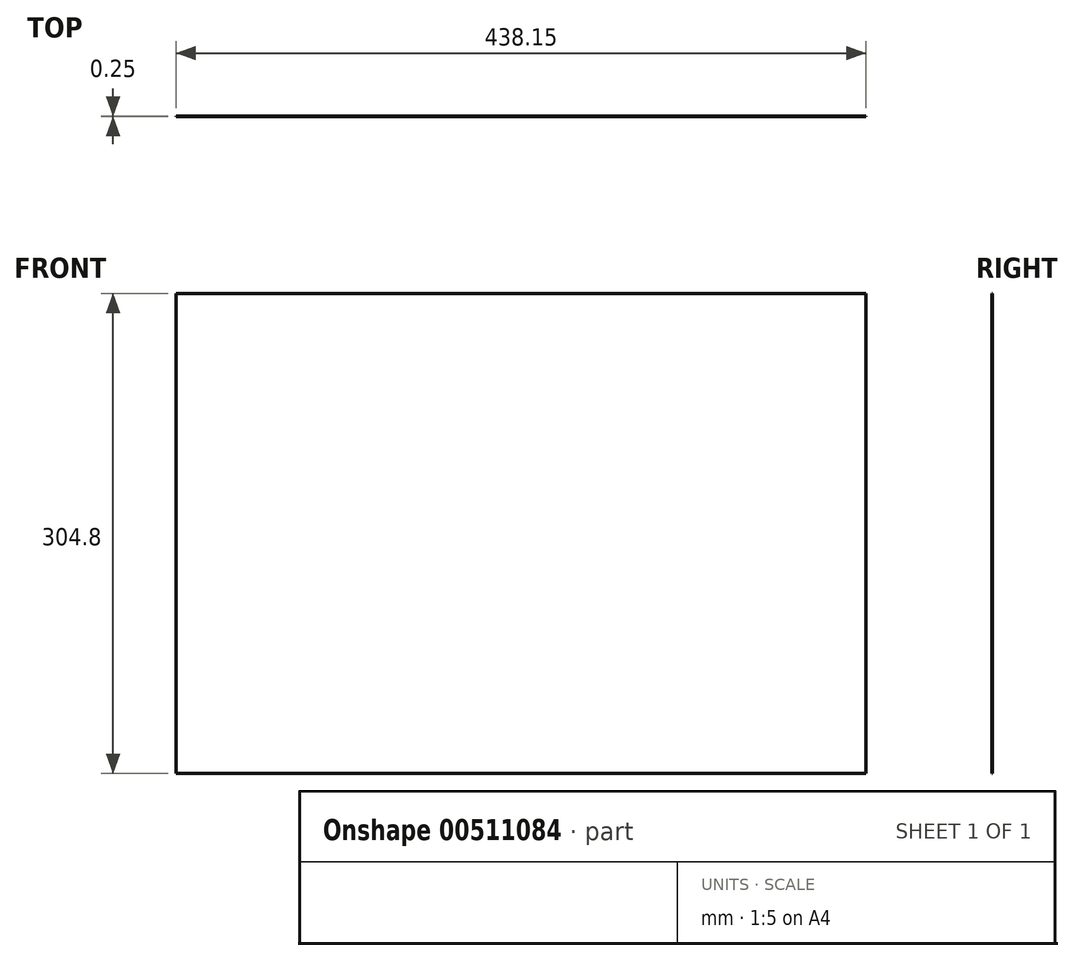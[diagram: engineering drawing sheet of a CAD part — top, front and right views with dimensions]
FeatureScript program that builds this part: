
annotation { "Feature Type Name" : "Feature", "Feature Type Description" : "" }
export const myFeature = defineFeature(function(context is Context, id is Id, definition is map)
    precondition{}
    {
        {
            assignVariable(context, id + "F0", {"name" : "plywoodThickness", "anyValue" : 0.25});
        }
        {
            var Q0;
            Q0=qCreatedBy(makeId("Front.planeOp"),FACE);
            var sketch = newSketch(context, id + "F1", { "sketchPlane" : qUnion([Q0])});
            skLineSegment(sketch, "E0.bottom", {"start": v(0, 0) * mm, "end": v(438.15, 0) * mm});
            skLineSegment(sketch, "E0.top", {"start": v(0, -304.8) * mm, "end": v(438.15, -304.8) * mm});
            skLineSegment(sketch, "E0.left", {"start": v(0, 0) * mm, "end": v(0, -304.8) * mm});
            skLineSegment(sketch, "E0.right", {"start": v(438.15, 0) * mm, "end": v(438.15, -304.8) * mm});
            skSolve(sketch);
        }
        {
            var Q0;
            Q0=makeQuery(id+"F1.imprint","IMPRINT",FACE,{"disambiguationData":[TD([[makeQuery(id+"F1.imprint","IMPRINT",EDGE,{"derivedFrom":sQuery(id+"F1.wireOp",EDGE,"E0.bottom")}),-1.0]])]});
            extrude(context, id + "F2", {"entities" : qUnion([Q0]), "depth" : (getVariable(context, 'plywoodThickness')) * mm, "offsetDistance" : 25.4 * mm});
        }
    });
